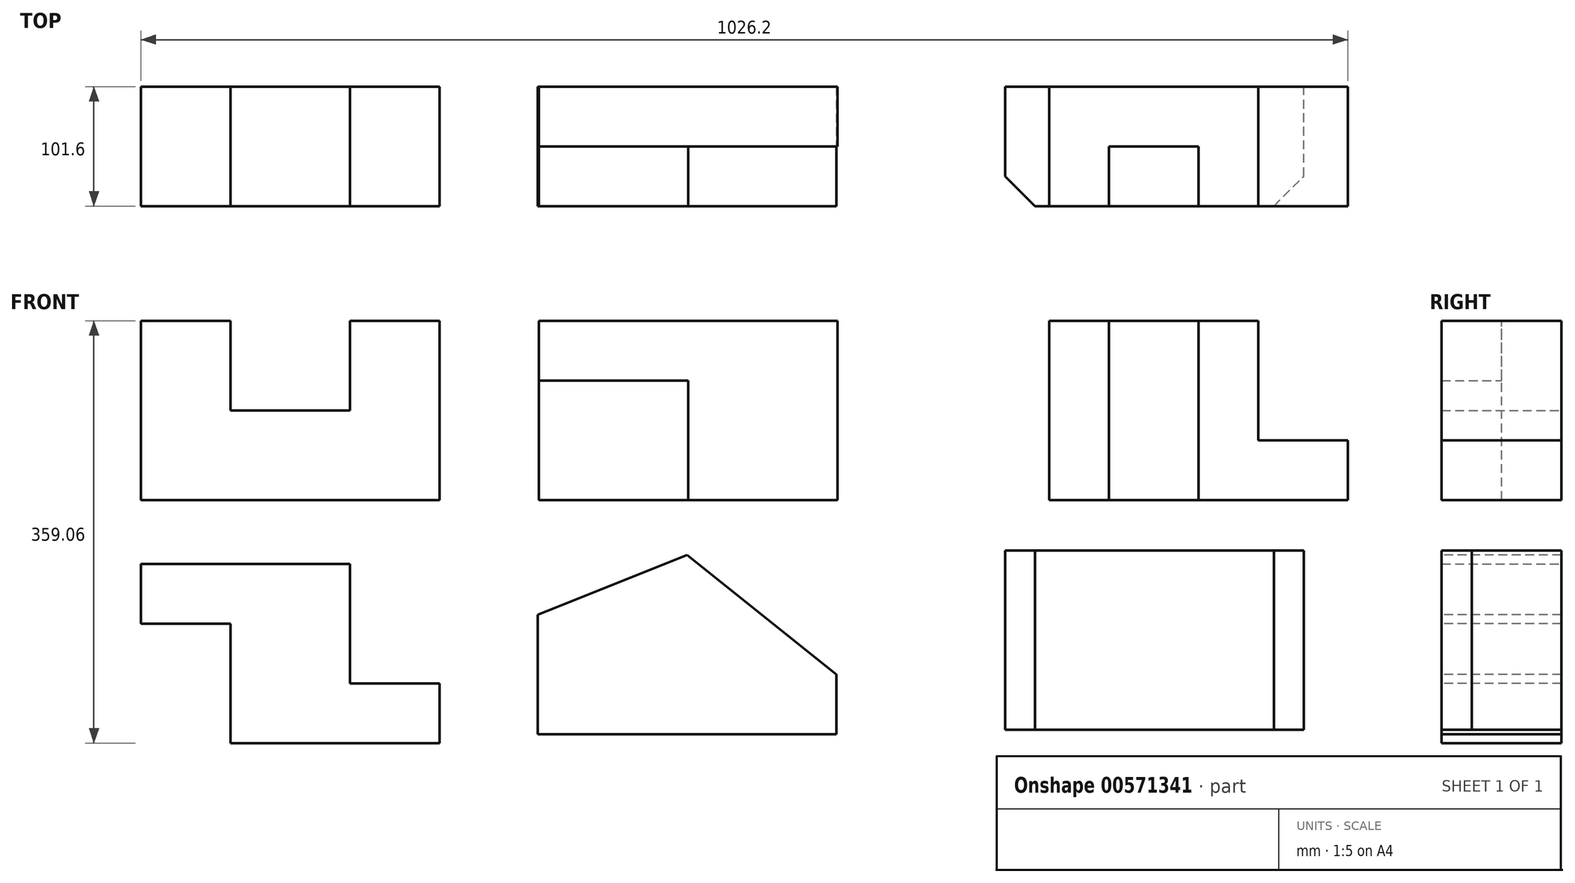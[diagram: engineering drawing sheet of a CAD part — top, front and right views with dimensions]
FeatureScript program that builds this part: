
annotation { "Feature Type Name" : "Feature", "Feature Type Description" : "" }
export const myFeature = defineFeature(function(context is Context, id is Id, definition is map)
    precondition{}
    {
        {
            var Q0;
            Q0=qCreatedBy(makeId("Front.planeOp"),FACE);
            var sketch = newSketch(context, id + "F0", { "sketchPlane" : qUnion([Q0])});
            skLineSegment(sketch, "E0", {"start": v(0, 0) * mm, "end": v(0, 152.4) * mm});
            skLineSegment(sketch, "E1", {"start": v(0, 152.4) * mm, "end": v(76.2, 152.4) * mm});
            skLineSegment(sketch, "E2", {"start": v(76.2, 152.4) * mm, "end": v(76.2, 76.2) * mm});
            skLineSegment(sketch, "E3", {"start": v(177.8, 76.2) * mm, "end": v(177.8, 152.4) * mm});
            skLineSegment(sketch, "E4", {"start": v(177.8, 152.4) * mm, "end": v(254, 152.4) * mm});
            skLineSegment(sketch, "E5", {"start": v(254, 152.4) * mm, "end": v(254, 0) * mm});
            skLineSegment(sketch, "E6", {"start": v(254, 0) * mm, "end": v(0, 0) * mm});
            skLineSegment(sketch, "E7", {"start": v(76.2, 76.2) * mm, "end": v(177.8, 76.2) * mm});
            skSolve(sketch);
        }
        {
            var Q0;
            Q0=makeQuery(id+"F0.imprint","IMPRINT",FACE,{"disambiguationData":[TD([[makeQuery(id+"F0.imprint","IMPRINT",EDGE,{"derivedFrom":sQuery(id+"F0.wireOp",EDGE,"E0")}),-1.0]])]});
            extrude(context, id + "F1", {"entities" : qUnion([Q0]), "depth" : 101.6 * mm, "offsetDistance" : 25.4 * mm});
        }
        {
            var Q0;
            Q0=qCreatedBy(makeId("Front.planeOp"),FACE);
            var sketch = newSketch(context, id + "F2", { "sketchPlane" : qUnion([Q0])});
            skLineSegment(sketch, "E8", {"start": v(338.34, 0) * mm, "end": v(338.34, 152.4) * mm});
            skLineSegment(sketch, "E9", {"start": v(338.34, 152.4) * mm, "end": v(592.34, 152.4) * mm});
            skLineSegment(sketch, "E10", {"start": v(592.34, 152.4) * mm, "end": v(592.34, 0) * mm});
            skLineSegment(sketch, "E11", {"start": v(592.34, 0) * mm, "end": v(338.34, 0) * mm});
            skSolve(sketch);
        }
        {
            var Q0;
            Q0=makeQuery(id+"F2.imprint","IMPRINT",FACE,{"disambiguationData":[TD([[makeQuery(id+"F2.imprint","IMPRINT",EDGE,{"derivedFrom":sQuery(id+"F2.wireOp",EDGE,"E8")}),-1.0]])]});
            extrude(context, id + "F3", {"entities" : qUnion([Q0]), "depth" : 101.6 * mm, "offsetDistance" : 25.4 * mm});
        }
        {
            var Q0;
            Q0=makeQuery(id+"F3.opExtrude","SWEPT_FACE",FACE,{"disambiguationData":[OSD([sQuery(id+"F2.wireOp",EDGE,"E9")])]});
            var sketch = newSketch(context, id + "F4", { "sketchPlane" : qUnion([Q0])});
            skLineSegment(sketch, "E12.bottom", {"start": v(592.34, -101.6) * mm, "end": v(465.34, -101.6) * mm});
            skLineSegment(sketch, "E12.top", {"start": v(592.34, -50.8) * mm, "end": v(465.34, -50.8) * mm});
            skLineSegment(sketch, "E12.left", {"start": v(592.34, -101.6) * mm, "end": v(592.34, -50.8) * mm});
            skLineSegment(sketch, "E12.right", {"start": v(465.34, -101.6) * mm, "end": v(465.34, -50.8) * mm});
            skLineSegment(sketch, "E13.bottom", {"start": v(338.34, -101.6) * mm, "end": v(465.34, -101.6) * mm});
            skLineSegment(sketch, "E13.top", {"start": v(338.34, -50.8) * mm, "end": v(465.34, -50.8) * mm});
            skLineSegment(sketch, "E13.left", {"start": v(338.34, -101.6) * mm, "end": v(338.34, -50.8) * mm});
            skSolve(sketch);
        }
        {
            var Q0;
            Q0=makeQuery(id+"F4.imprint","IMPRINT",FACE,{"disambiguationData":[TD([[makeQuery(id+"F4.imprint","IMPRINT",EDGE,{"derivedFrom":sQuery(id+"F4.wireOp",EDGE,"E12.bottom")}),1.0]])]});
            extrude(context, id + "F5", {"entities" : qUnion([Q0]), "operationType" : NewBodyOperationType.REMOVE, "oppositeDirection" : true, "depth" : 152.4 * mm, "offsetDistance" : 25.4 * mm});
        }
        {
            var Q0;
            Q0=makeQuery(id+"F3.opExtrude","SWEPT_FACE",FACE,{"disambiguationData":[OSD([sQuery(id+"F2.wireOp",EDGE,"E9")])]});
            var sketch = newSketch(context, id + "F6", { "sketchPlane" : qUnion([Q0])});
            skLineSegment(sketch, "E14.bottom", {"start": v(338.34, -101.6) * mm, "end": v(465.34, -101.6) * mm});
            skLineSegment(sketch, "E14.top", {"start": v(338.34, -50.8) * mm, "end": v(465.34, -50.8) * mm});
            skLineSegment(sketch, "E14.left", {"start": v(338.34, -101.6) * mm, "end": v(338.34, -50.8) * mm});
            skLineSegment(sketch, "E14.right", {"start": v(465.34, -101.6) * mm, "end": v(465.34, -50.8) * mm});
            skSolve(sketch);
        }
        {
            var Q0;
            Q0=makeQuery(id+"F6.imprint","IMPRINT",FACE,{"disambiguationData":[TD([[makeQuery(id+"F6.imprint","IMPRINT",EDGE,{"derivedFrom":sQuery(id+"F6.wireOp",EDGE,"E14.bottom")}),1.0]])]});
            extrude(context, id + "F7", {"entities" : qUnion([Q0]), "operationType" : NewBodyOperationType.REMOVE, "oppositeDirection" : true, "depth" : 50.8 * mm, "offsetDistance" : 25.4 * mm});
        }
        {
            var Q0;
            Q0=qCreatedBy(makeId("Front.planeOp"),FACE);
            var sketch = newSketch(context, id + "F8", { "sketchPlane" : qUnion([Q0])});
            skLineSegment(sketch, "E15", {"start": v(772.2, 0) * mm, "end": v(772.2, 152.4) * mm});
            skLineSegment(sketch, "E16", {"start": v(772.2, 152.4) * mm, "end": v(1026.2, 152.4) * mm});
            skLineSegment(sketch, "E17", {"start": v(1026.2, 152.4) * mm, "end": v(1026.2, 0) * mm});
            skLineSegment(sketch, "E18", {"start": v(1026.2, 0) * mm, "end": v(772.2, 0) * mm});
            skSolve(sketch);
        }
        {
            var Q0;
            Q0=makeQuery(id+"F8.imprint","IMPRINT",FACE,{"disambiguationData":[TD([[makeQuery(id+"F8.imprint","IMPRINT",EDGE,{"derivedFrom":sQuery(id+"F8.wireOp",EDGE,"E15")}),-1.0]])]});
            extrude(context, id + "F9", {"entities" : qUnion([Q0]), "depth" : 101.6 * mm, "offsetDistance" : 25.4 * mm});
        }
        {
            var Q0;
            Q0=makeQuery(id+"F9.opExtrude","SWEPT_FACE",FACE,{"disambiguationData":[OSD([sQuery(id+"F8.wireOp",EDGE,"E16")])]});
            var sketch = newSketch(context, id + "F10", { "sketchPlane" : qUnion([Q0])});
            skLineSegment(sketch, "E19", {"start": v(772.2, -101.6) * mm, "end": v(823, -101.6) * mm});
            skLineSegment(sketch, "E20.bottom", {"start": v(823, -101.6) * mm, "end": v(899.2, -101.6) * mm});
            skLineSegment(sketch, "E20.top", {"start": v(823, -50.8) * mm, "end": v(899.2, -50.8) * mm});
            skLineSegment(sketch, "E20.left", {"start": v(823, -101.6) * mm, "end": v(823, -50.8) * mm});
            skLineSegment(sketch, "E20.right", {"start": v(899.2, -101.6) * mm, "end": v(899.2, -50.8) * mm});
            skLineSegment(sketch, "E21.bottom", {"start": v(1026.2, -101.6) * mm, "end": v(950, -101.6) * mm});
            skLineSegment(sketch, "E21.top", {"start": v(1026.2, 0) * mm, "end": v(950, 0) * mm});
            skLineSegment(sketch, "E21.left", {"start": v(1026.2, -101.6) * mm, "end": v(1026.2, 0) * mm});
            skLineSegment(sketch, "E21.right", {"start": v(950, -101.6) * mm, "end": v(950, 0) * mm});
            skSolve(sketch);
        }
        {
            var Q0;
            Q0=makeQuery(id+"F10.imprint","IMPRINT",FACE,{"disambiguationData":[TD([[makeQuery(id+"F10.imprint","IMPRINT",EDGE,{"derivedFrom":sQuery(id+"F10.wireOp",EDGE,"E20.bottom")}),1.0]])]});
            extrude(context, id + "F11", {"entities" : qUnion([Q0]), "operationType" : NewBodyOperationType.REMOVE, "oppositeDirection" : true, "depth" : 152.4 * mm, "offsetDistance" : 25.4 * mm});
        }
        {
            var Q0;
            Q0=makeQuery(id+"F9.opExtrude","SWEPT_FACE",FACE,{"disambiguationData":[OSD([sQuery(id+"F8.wireOp",EDGE,"E16")])]});
            var sketch = newSketch(context, id + "F12", { "sketchPlane" : qUnion([Q0])});
            skLineSegment(sketch, "E22.bottom", {"start": v(1026.2, -101.6) * mm, "end": v(950, -101.6) * mm});
            skLineSegment(sketch, "E22.top", {"start": v(1026.2, 0) * mm, "end": v(950, 0) * mm});
            skLineSegment(sketch, "E22.left", {"start": v(1026.2, -101.6) * mm, "end": v(1026.2, 0) * mm});
            skLineSegment(sketch, "E22.right", {"start": v(950, -101.6) * mm, "end": v(950, 0) * mm});
            skSolve(sketch);
        }
        {
            var Q0;
            Q0=makeQuery(id+"F12.imprint","IMPRINT",FACE,{"disambiguationData":[TD([[makeQuery(id+"F12.imprint","IMPRINT",EDGE,{"derivedFrom":sQuery(id+"F12.wireOp",EDGE,"E22.bottom")}),1.0]])]});
            extrude(context, id + "F13", {"entities" : qUnion([Q0]), "operationType" : NewBodyOperationType.REMOVE, "oppositeDirection" : true, "depth" : 101.6 * mm, "offsetDistance" : 25.4 * mm});
        }
        {
            var Q0;
            Q0=qCreatedBy(makeId("Front.planeOp"),FACE);
            var sketch = newSketch(context, id + "F14", { "sketchPlane" : qUnion([Q0])});
            skLineSegment(sketch, "E23", {"start": v(0, -54.26) * mm, "end": v(254, -54.26) * mm});
            skLineSegment(sketch, "E24", {"start": v(254, -54.26) * mm, "end": v(254, -206.66) * mm});
            skLineSegment(sketch, "E25", {"start": v(254, -206.66) * mm, "end": v(0, -206.66) * mm});
            skLineSegment(sketch, "E26", {"start": v(0, -206.66) * mm, "end": v(0, -54.26) * mm});
            skSolve(sketch);
        }
        {
            var Q0;
            Q0=makeQuery(id+"F14.imprint","IMPRINT",FACE,{"disambiguationData":[TD([[makeQuery(id+"F14.imprint","IMPRINT",EDGE,{"derivedFrom":sQuery(id+"F14.wireOp",EDGE,"E23")}),-1.0]])]});
            extrude(context, id + "F15", {"entities" : qUnion([Q0]), "depth" : 101.6 * mm, "offsetDistance" : 25.4 * mm});
        }
        {
            var Q0;
            Q0=makeQuery(id+"F15.opExtrude","CAP_FACE",FACE,{"disambiguationData":[OSD([sQuery(id+"F14.wireOp",EDGE,"E23"),sQuery(id+"F14.wireOp",EDGE,"E24"),sQuery(id+"F14.wireOp",EDGE,"E25"),sQuery(id+"F14.wireOp",EDGE,"E26")])],"isStart":false});
            var sketch = newSketch(context, id + "F16", { "sketchPlane" : qUnion([Q0])});
            skLineSegment(sketch, "E27.bottom", {"start": v(0, -206.66) * mm, "end": v(76.2, -206.66) * mm});
            skLineSegment(sketch, "E27.top", {"start": v(0, -105.06) * mm, "end": v(76.2, -105.06) * mm});
            skLineSegment(sketch, "E27.left", {"start": v(0, -206.66) * mm, "end": v(0, -105.06) * mm});
            skLineSegment(sketch, "E27.right", {"start": v(76.2, -206.66) * mm, "end": v(76.2, -105.06) * mm});
            skSolve(sketch);
        }
        {
            var Q0;
            Q0=makeQuery(id+"F16.imprint","IMPRINT",FACE,{"disambiguationData":[TD([[makeQuery(id+"F16.imprint","IMPRINT",EDGE,{"derivedFrom":sQuery(id+"F16.wireOp",EDGE,"E27.bottom")}),-1.0]])]});
            extrude(context, id + "F17", {"entities" : qUnion([Q0]), "operationType" : NewBodyOperationType.REMOVE, "oppositeDirection" : true, "depth" : 101.6 * mm, "offsetDistance" : 25.4 * mm});
        }
        {
            var Q0;
            Q0=makeQuery(id+"F15.opExtrude","CAP_FACE",FACE,{"disambiguationData":[OSD([sQuery(id+"F14.wireOp",EDGE,"E23"),sQuery(id+"F14.wireOp",EDGE,"E24"),sQuery(id+"F14.wireOp",EDGE,"E25"),sQuery(id+"F14.wireOp",EDGE,"E26")])],"isStart":false});
            var sketch = newSketch(context, id + "F18", { "sketchPlane" : qUnion([Q0])});
            skLineSegment(sketch, "E28.bottom", {"start": v(254, -54.26) * mm, "end": v(177.8, -54.26) * mm});
            skLineSegment(sketch, "E28.top", {"start": v(254, -155.86) * mm, "end": v(177.8, -155.86) * mm});
            skLineSegment(sketch, "E28.left", {"start": v(254, -54.26) * mm, "end": v(254, -155.86) * mm});
            skLineSegment(sketch, "E28.right", {"start": v(177.8, -54.26) * mm, "end": v(177.8, -155.86) * mm});
            skSolve(sketch);
        }
        {
            var Q0;
            Q0=makeQuery(id+"F18.imprint","IMPRINT",FACE,{"disambiguationData":[TD([[makeQuery(id+"F18.imprint","IMPRINT",EDGE,{"derivedFrom":sQuery(id+"F18.wireOp",EDGE,"E28.bottom")}),-1.0]])]});
            extrude(context, id + "F19", {"entities" : qUnion([Q0]), "operationType" : NewBodyOperationType.REMOVE, "oppositeDirection" : true, "depth" : 101.6 * mm, "offsetDistance" : 25.4 * mm});
        }
        {
            var Q0;
            Q0=qCreatedBy(makeId("Front.planeOp"),FACE);
            var sketch = newSketch(context, id + "F20", { "sketchPlane" : qUnion([Q0])});
            skLineSegment(sketch, "E29", {"start": v(337.5, -199.1) * mm, "end": v(337.5, -46.7) * mm});
            skLineSegment(sketch, "E30", {"start": v(337.5, -46.7) * mm, "end": v(591.5, -46.7) * mm});
            skLineSegment(sketch, "E31", {"start": v(337.5, -199.1) * mm, "end": v(591.5, -199.1) * mm});
            skLineSegment(sketch, "E32", {"start": v(591.5, -46.7) * mm, "end": v(591.5, -199.1) * mm});
            skSolve(sketch);
        }
        {
            var Q0;
            Q0=makeQuery(id+"F20.imprint","IMPRINT",FACE,{"disambiguationData":[TD([[makeQuery(id+"F20.imprint","IMPRINT",EDGE,{"derivedFrom":sQuery(id+"F20.wireOp",EDGE,"E29")}),-1.0]])]});
            extrude(context, id + "F21", {"entities" : qUnion([Q0]), "depth" : 101.6 * mm, "offsetDistance" : 25.4 * mm});
        }
        {
            var Q0;
            Q0=makeQuery(id+"F21.opExtrude","CAP_FACE",FACE,{"disambiguationData":[OSD([sQuery(id+"F20.wireOp",EDGE,"E29"),sQuery(id+"F20.wireOp",EDGE,"E30"),sQuery(id+"F20.wireOp",EDGE,"E31"),sQuery(id+"F20.wireOp",EDGE,"E32")])],"isStart":false});
            var sketch = newSketch(context, id + "F22", { "sketchPlane" : qUnion([Q0])});
            skLineSegment(sketch, "E33", {"start": v(337.5, -46.7) * mm, "end": v(337.5, -97.5) * mm});
            skLineSegment(sketch, "E34", {"start": v(337.5, -46.7) * mm, "end": v(464.5, -46.7) * mm});
            skLineSegment(sketch, "E35", {"start": v(464.5, -46.7) * mm, "end": v(337.5, -97.5) * mm});
            skSolve(sketch);
        }
        {
            var Q0;
            Q0=makeQuery(id+"F22.imprint","IMPRINT",FACE,{"disambiguationData":[TD([[makeQuery(id+"F22.imprint","IMPRINT",EDGE,{"derivedFrom":sQuery(id+"F22.wireOp",EDGE,"E33")}),-1.0]])]});
            extrude(context, id + "F23", {"entities" : qUnion([Q0]), "operationType" : NewBodyOperationType.REMOVE, "oppositeDirection" : true, "depth" : 101.6 * mm, "offsetDistance" : 25.4 * mm});
        }
        {
            var Q0;
            Q0=makeQuery(id+"F21.opExtrude","CAP_FACE",FACE,{"disambiguationData":[OSD([sQuery(id+"F20.wireOp",EDGE,"E29"),sQuery(id+"F20.wireOp",EDGE,"E30"),sQuery(id+"F20.wireOp",EDGE,"E31"),sQuery(id+"F20.wireOp",EDGE,"E32")])],"isStart":false});
            var sketch = newSketch(context, id + "F24", { "sketchPlane" : qUnion([Q0])});
            skLineSegment(sketch, "E36", {"start": v(591.5, -46.7) * mm, "end": v(591.5, -148.3) * mm});
            skLineSegment(sketch, "E37", {"start": v(591.5, -46.7) * mm, "end": v(464.5, -46.7) * mm});
            skLineSegment(sketch, "E38", {"start": v(591.5, -148.3) * mm, "end": v(464.5, -46.7) * mm});
            skSolve(sketch);
        }
        {
            var Q0;
            Q0=makeQuery(id+"F24.imprint","IMPRINT",FACE,{"disambiguationData":[TD([[makeQuery(id+"F24.imprint","IMPRINT",EDGE,{"derivedFrom":sQuery(id+"F24.wireOp",EDGE,"E36")}),-1.0]])]});
            extrude(context, id + "F25", {"entities" : qUnion([Q0]), "operationType" : NewBodyOperationType.REMOVE, "oppositeDirection" : true, "depth" : 101.6 * mm, "offsetDistance" : 25.4 * mm});
        }
        {
            var Q0;
            Q0=qCreatedBy(makeId("Front.planeOp"),FACE);
            var sketch = newSketch(context, id + "F26", { "sketchPlane" : qUnion([Q0])});
            skLineSegment(sketch, "E39", {"start": v(734.75, -195.35) * mm, "end": v(734.75, -42.95) * mm});
            skLineSegment(sketch, "E40", {"start": v(734.75, -42.95) * mm, "end": v(988.75, -42.95) * mm});
            skLineSegment(sketch, "E41", {"start": v(734.75, -195.35) * mm, "end": v(988.75, -195.35) * mm});
            skLineSegment(sketch, "E42", {"start": v(988.75, -195.35) * mm, "end": v(988.75, -42.95) * mm});
            skSolve(sketch);
        }
        {
            var Q0;
            Q0=makeQuery(id+"F26.imprint","IMPRINT",FACE,{"disambiguationData":[TD([[makeQuery(id+"F26.imprint","IMPRINT",EDGE,{"derivedFrom":sQuery(id+"F26.wireOp",EDGE,"E39")}),-1.0]])]});
            extrude(context, id + "F27", {"entities" : qUnion([Q0]), "depth" : 101.6 * mm, "offsetDistance" : 25.4 * mm});
        }
        {
            var Q0;
            Q0=makeQuery(id+"F27.opExtrude","SWEPT_FACE",FACE,{"disambiguationData":[OSD([sQuery(id+"F26.wireOp",EDGE,"E41")])]});
            var sketch = newSketch(context, id + "F28", { "sketchPlane" : qUnion([Q0])});
            skLineSegment(sketch, "E43", {"start": v(734.75, 101.6) * mm, "end": v(734.75, 76.2) * mm});
            skLineSegment(sketch, "E44", {"start": v(734.75, 101.6) * mm, "end": v(760.15, 101.6) * mm});
            skLineSegment(sketch, "E45", {"start": v(734.75, 76.2) * mm, "end": v(760.15, 101.6) * mm});
            skLineSegment(sketch, "E46", {"start": v(988.75, 101.6) * mm, "end": v(963.35, 101.6) * mm});
            skLineSegment(sketch, "E47", {"start": v(988.75, 101.6) * mm, "end": v(988.75, 76.2) * mm});
            skLineSegment(sketch, "E48", {"start": v(963.35, 101.6) * mm, "end": v(988.75, 76.2) * mm});
            skSolve(sketch);
        }
        {
            var Q0;
            Q0=makeQuery(id+"F28.imprint","IMPRINT",FACE,{"disambiguationData":[TD([[makeQuery(id+"F28.imprint","IMPRINT",EDGE,{"derivedFrom":sQuery(id+"F28.wireOp",EDGE,"E43")}),1.0]])]});
            var Q1;
            Q1=makeQuery(id+"F28.imprint","IMPRINT",FACE,{"disambiguationData":[TD([[makeQuery(id+"F28.imprint","IMPRINT",EDGE,{"derivedFrom":sQuery(id+"F28.wireOp",EDGE,"E46")}),-1.0]])]});
            extrude(context, id + "F29", {"entities" : qUnion([Q0, Q1]), "operationType" : NewBodyOperationType.REMOVE, "oppositeDirection" : true, "depth" : 152.4 * mm, "offsetDistance" : 25.4 * mm});
        }
    });
